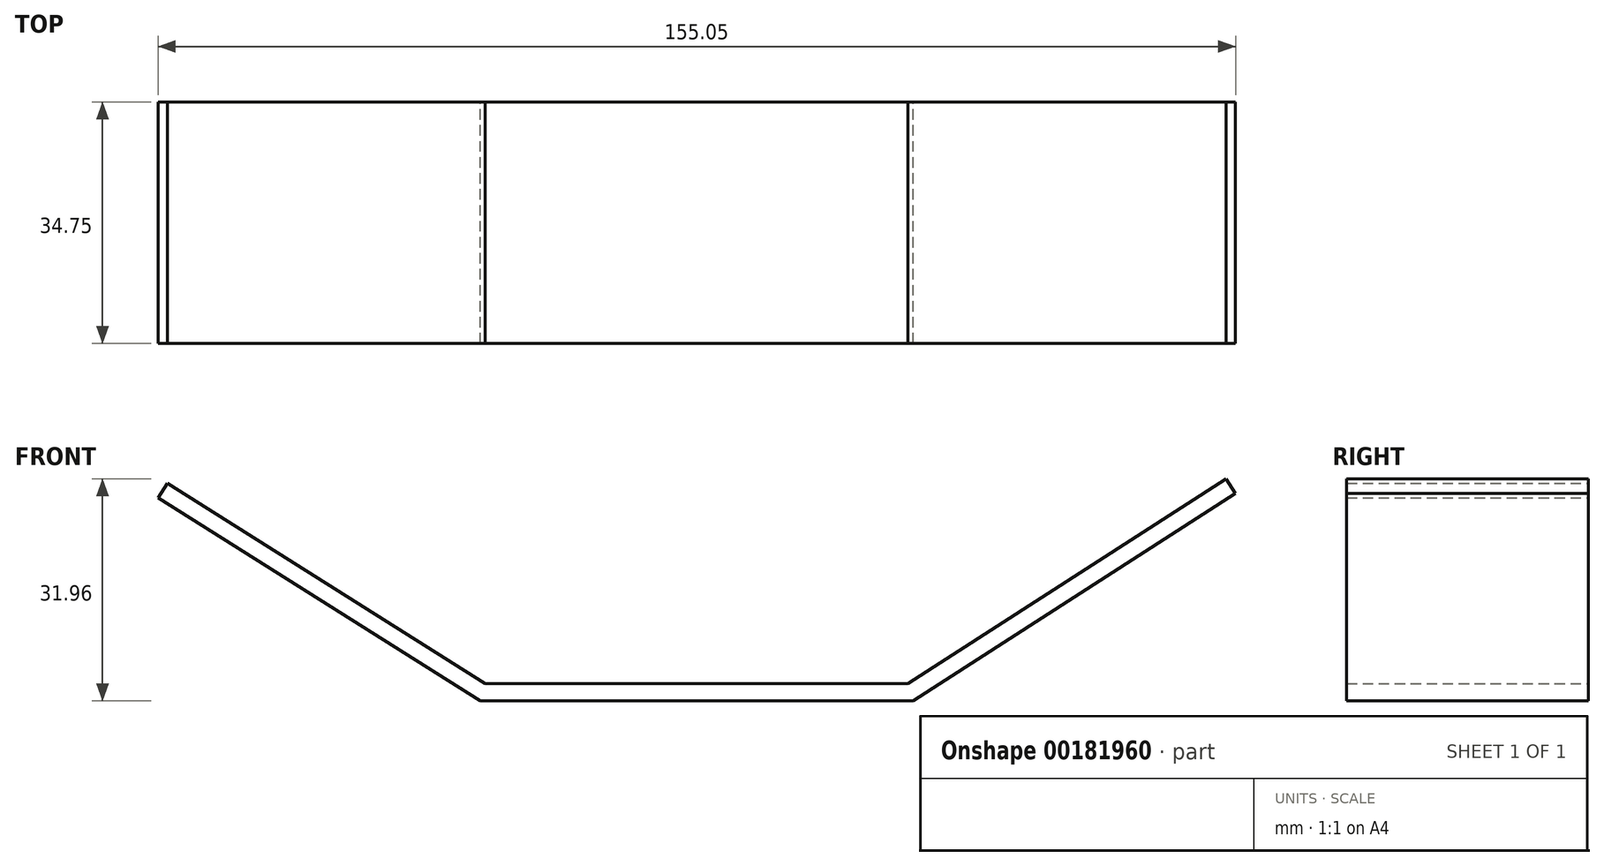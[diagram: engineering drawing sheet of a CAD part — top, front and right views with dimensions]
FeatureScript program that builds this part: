
annotation { "Feature Type Name" : "Feature", "Feature Type Description" : "" }
export const myFeature = defineFeature(function(context is Context, id is Id, definition is map)
    precondition{}
    {
        {
            var Q0;
            Q0=qCreatedBy(makeId("Front.planeOp"),FACE);
            var sketch = newSketch(context, id + "F0", { "sketchPlane" : qUnion([Q0])});
            skLineSegment(sketch, "E0", {"start": v(-30.3, 0) * mm, "end": v(30.52, 0) * mm});
            skLineSegment(sketch, "E1", {"start": v(30.52, 0) * mm, "end": v(-30.3, 0) * mm});
            skLineSegment(sketch, "E2", {"start": v(-30.3, 0) * mm, "end": v(-76.08, 28.84) * mm});
            skLineSegment(sketch, "E3", {"start": v(-76.08, 28.84) * mm, "end": v(-30.3, 0) * mm});
            skLineSegment(sketch, "E4", {"start": v(30.52, 0) * mm, "end": v(76.3, 29.47) * mm});
            skLineSegment(sketch, "E5.0", {"start": v(31.25, -2.49) * mm, "end": v(77.64, 27.38) * mm});
            skLineSegment(sketch, "E5.1", {"start": v(31.25, -2.49) * mm, "end": v(-31.03, -2.49) * mm});
            skLineSegment(sketch, "E5.2", {"start": v(-77.4, 26.74) * mm, "end": v(-31.03, -2.49) * mm});
            skLineSegment(sketch, "E6", {"start": v(-76.08, 28.84) * mm, "end": v(-77.4, 26.74) * mm});
            skLineSegment(sketch, "E7", {"start": v(76.3, 29.47) * mm, "end": v(77.64, 27.38) * mm});
            skSolve(sketch);
        }
        {
            var Q0;
            Q0 = qSketchRegion(id + "F0", true);
            extrude(context, id + "F1", {"entities" : qUnion([Q0]), "depth" : 34.75 * mm});
        }
    });
